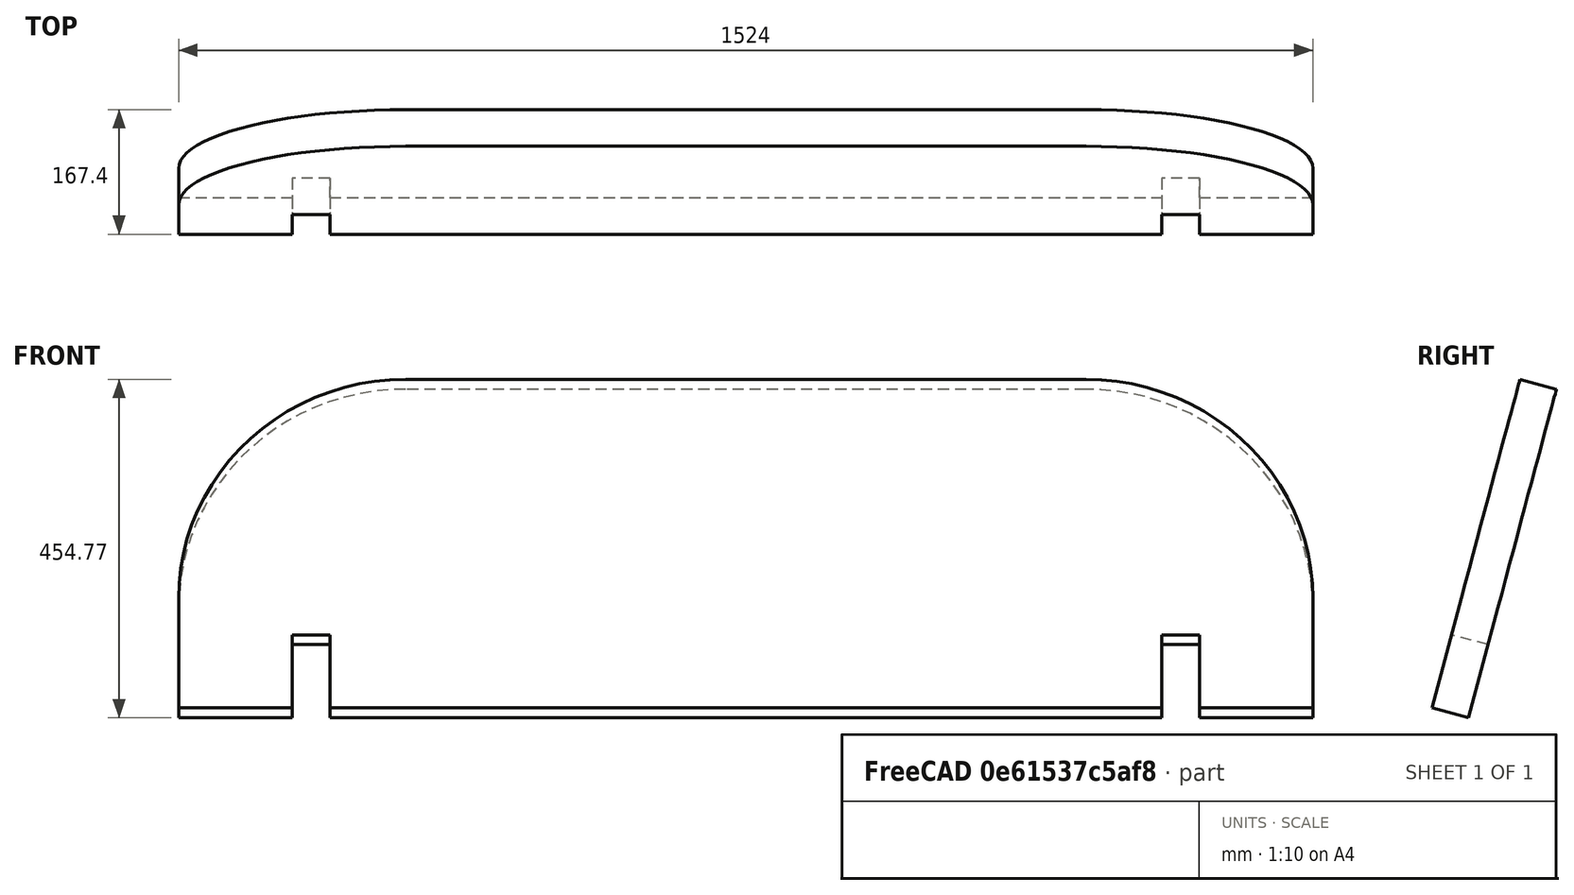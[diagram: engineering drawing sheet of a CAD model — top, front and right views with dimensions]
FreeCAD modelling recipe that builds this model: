
FCSTD DOCUMENT  (FreeCAD 0.21R33771 (Git))
Label: eclipse-2-back
License: All rights reserved
LicenseURL: http://en.wikipedia.org/wiki/All_rights_reserved
objects: Sketcher::SketchObject×1, PartDesign::Pad×1, PartDesign::Body×1, Spreadsheet::Sheet×1
note: 4 computed .brp shape members not serialized (recipe doc carries the construction recipe); baked Part::Feature solids carry a one-line shape summary decoded from their .brp

FEATURE [Sketcher::SketchObject] Sketch003
  FullyConstrained = false
  MapMode = 5
  Placement = pos=(0,0,0) rot=(1,0,0;1.5708rad)
  Support = -> [XZ_Plane003]
  expr: Constraints[11] = <<dims>>.eclipse_length + <<dims>>.eclipse_height
  expr: Constraints[12] = <<dims>>.eclipse_height / 2
  expr: Constraints[13] = <<dims>>.eclipse_height * 3 / 4
  expr: Constraints[18] = <<dims>>.thickness
  expr: Constraints[31] = <<dims>>.thickness
  sketch-geometry (15):
    g0: LineSegment StartX=-130.38 StartY=312.133 StartZ=0 EndX=-130.38 EndY=159.733 EndZ=0
    g1: LineSegment StartX=-130.38 StartY=159.733 StartZ=0 EndX=22.0201 EndY=159.733 EndZ=0
    g2: LineSegment StartX=1393.62 StartY=159.733 StartZ=0 EndX=1393.62 EndY=312.133 EndZ=0
    g3: LineSegment StartX=1088.82 StartY=616.933 StartZ=0 EndX=174.42 EndY=616.933 EndZ=0
    g4: GeomPoint X=616.792 Y=511.343 Z=0
    g5: ArcOfCircle CenterX=174.42 CenterY=312.133 CenterZ=0 NormalX=0 NormalY=0 NormalZ=1 AngleXU=0 Radius=304.8 StartAngle=1.5708 EndAngle=3.14159
    g6: ArcOfCircle CenterX=1088.82 CenterY=312.133 CenterZ=0 NormalX=0 NormalY=0 NormalZ=1 AngleXU=0 Radius=304.8 StartAngle=3e-16 EndAngle=1.5708
    g7: LineSegment StartX=72.8201 StartY=159.733 StartZ=0 EndX=72.8201 EndY=261.333 EndZ=0
    g8: LineSegment StartX=72.8201 StartY=261.333 StartZ=0 EndX=22.0201 EndY=261.333 EndZ=0
    g9: LineSegment StartX=22.0201 StartY=261.333 StartZ=0 EndX=22.0201 EndY=159.733 EndZ=0
    g10: LineSegment StartX=1241.22 StartY=159.733 StartZ=0 EndX=1241.22 EndY=261.333 EndZ=0
    g11: LineSegment StartX=1241.22 StartY=261.333 StartZ=0 EndX=1190.42 EndY=261.333 EndZ=0
    g12: LineSegment StartX=1190.42 StartY=261.333 StartZ=0 EndX=1190.42 EndY=159.733 EndZ=0
    g13: LineSegment StartX=72.8201 StartY=159.733 StartZ=0 EndX=1190.42 EndY=159.733 EndZ=0
    g14: LineSegment StartX=1241.22 StartY=159.733 StartZ=0 EndX=1393.62 EndY=159.733 EndZ=0
  constraints (36):
    c: Coincident(g0,g1)
    c: Coincident(g14,g2)
    c: Horizontal(g1)
    c: Horizontal(g3)
    c: Vertical(g0)
    c: Vertical(g2)
    c: Tangent(g3,g5) = -1.5708
    c: Tangent(g0,g5) = -1.5708
    c: Tangent(g3,g6) = -1.5708
    c: Tangent(g2,g6) = -1.5708
    c: Equal(g5,g6)
    c: DistanceX(g1,g14) = 1524
    c: Radius(g5) = 304.8
    c: DistanceY(g0,g3) = 457.2
    c: Vertical(g7)
    c: Coincident(g8,g7)
    c: Horizontal(g8)
    c: Vertical(g9)
    c: DistanceX(g8,g7) = 50.8
    c: Coincident(g8,g9)
    c: DistanceX(g0,g9) = 152.4
    c: DistanceY(g9,g9) = 101.6
    c: PointOnObject(g10,g1)
    c: Vertical(g10)
    c: PointOnObject(g12,g1)
    c: Vertical(g12)
    c: Horizontal(g11)
    c: Coincident(g12,g11)
    c: Coincident(g10,g11)
    c: DistanceY(g12,g12) = 101.6
    c: DistanceX(g10,g14) = 152.4
    c: DistanceX(g11,g10) = 50.8
    c: Coincident(g1,g9)
    c: Coincident(g13,g7)
    c: PointOnObject(g13,g12)
    c: PointOnObject(g14,g10)
FEATURE [PartDesign::Pad] Pad003
  Direction = (0,-1,-2e-16)
  Length = 50.8
  Length2 = 10
  Placement = pos=(0,0,0) rot=(1,0,0;1.5708rad)
  Profile = -> Sketch003
  ReferenceAxis = -> Sketch003 [N_Axis]
  Type = 0
  expr: Length = <<dims>>.thickness
FEATURE [PartDesign::Body] Body003
  Group = -> [Sketch003,Pad003]
  Origin = -> Origin003
  Placement = pos=(0,183.717,-79.4696) rot=(-1,0,0;0.261799rad)
  Tip = -> Pad003
FEATURE [Spreadsheet::Sheet] Spreadsheet  label="dims"
  cells = B2='eclipse_length; C2(eclipse_length)==36 in; B3='eclipse_height; C3(eclipse_height)==24 in; B4='thickness; C4(thickness)==2 in; B5='slot_from_end; C5(slot_from_end)==6 in; B6='seat_length; C6(seat_length)==48 in
